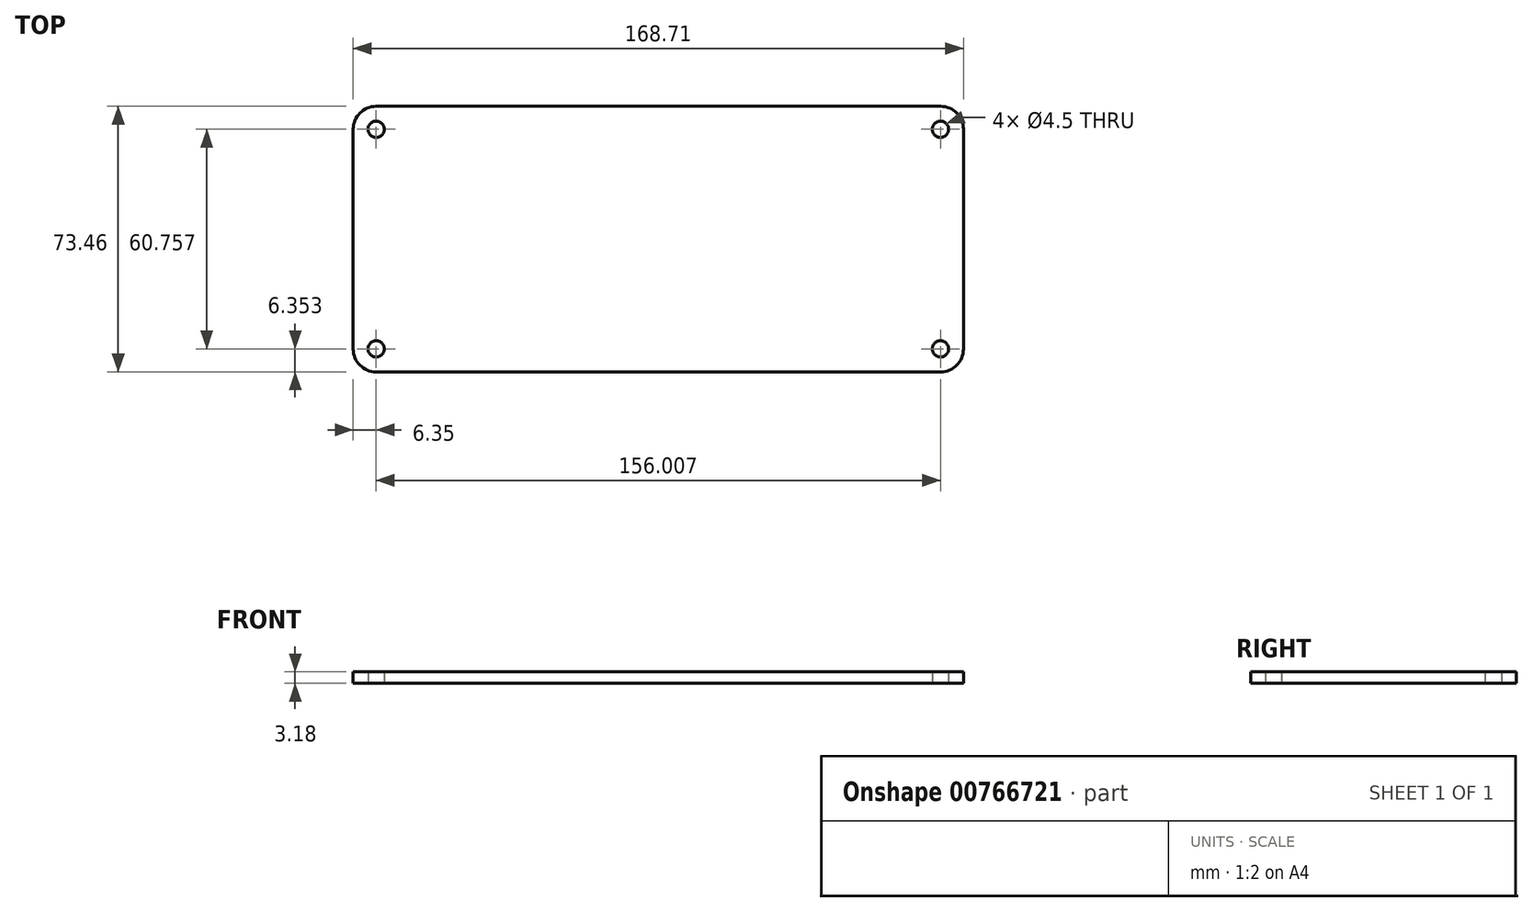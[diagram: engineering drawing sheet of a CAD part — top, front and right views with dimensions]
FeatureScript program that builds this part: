
annotation { "Feature Type Name" : "Feature", "Feature Type Description" : "" }
export const myFeature = defineFeature(function(context is Context, id is Id, definition is map)
    precondition{}
    {
        {
            var Q0;
            Q0=qCreatedBy(makeId("Top.planeOp"),FACE);
            var sketch = newSketch(context, id + "F0", { "sketchPlane" : qUnion([Q0])});
            skLineSegment(sketch, "E0.bottom", {"start": v(6.35, 0) * mm, "end": v(162.36, 0) * mm});
            skLineSegment(sketch, "E0.top", {"start": v(6.35, -73.46) * mm, "end": v(162.36, -73.46) * mm});
            skLineSegment(sketch, "E0.left", {"start": v(0, -6.35) * mm, "end": v(0, -67.1) * mm});
            skLineSegment(sketch, "E0.right", {"start": v(168.7, -6.35) * mm, "end": v(168.7, -67.1) * mm});
            skCircle(sketch, "E1", {"center": v(6.35, -6.35) * mm, "radius": 2.25 * mm});
            skCircle(sketch, "E2", {"center": v(6.35, -67.1) * mm, "radius": 2.25 * mm});
            skCircle(sketch, "E3", {"center": v(162.36, -6.35) * mm, "radius": 2.25 * mm});
            skCircle(sketch, "E4", {"center": v(162.36, -67.1) * mm, "radius": 2.25 * mm});
            skPoint(sketch, "E5.visualSharp", {"position": v(0, 0) * mm});
            skArc(sketch, "E5.filletArc", {"start": v(6.35, 0) * mm, "mid": v(1.86, -1.86) * mm, "end": v(0, -6.35) * mm});
            skPoint(sketch, "E6.visualSharp", {"position": v(0, -73.46) * mm});
            skArc(sketch, "E6.filletArc", {"start": v(0, -67.1) * mm, "mid": v(1.86, -71.6) * mm, "end": v(6.35, -73.46) * mm});
            skPoint(sketch, "E7.visualSharp", {"position": v(168.7, 0) * mm});
            skArc(sketch, "E7.filletArc", {"start": v(168.7, -6.35) * mm, "mid": v(166.85, -1.86) * mm, "end": v(162.36, 0) * mm});
            skPoint(sketch, "E8.visualSharp", {"position": v(168.7, -73.46) * mm});
            skArc(sketch, "E8.filletArc", {"start": v(162.36, -73.46) * mm, "mid": v(166.85, -71.6) * mm, "end": v(168.7, -67.1) * mm});
            skSolve(sketch);
        }
        {
            var Q0;
            Q0=makeQuery(id+"F0.imprint","IMPRINT",FACE,{"disambiguationData":[TD([[makeQuery(id+"F0.imprint","IMPRINT",EDGE,{"derivedFrom":sQuery(id+"F0.wireOp",EDGE,"E0.bottom")}),-1.0]])]});
            extrude(context, id + "F1", {"entities" : qUnion([Q0]), "depth" : 3.17 * mm, "offsetDistance" : 25.4 * mm});
        }
    });
